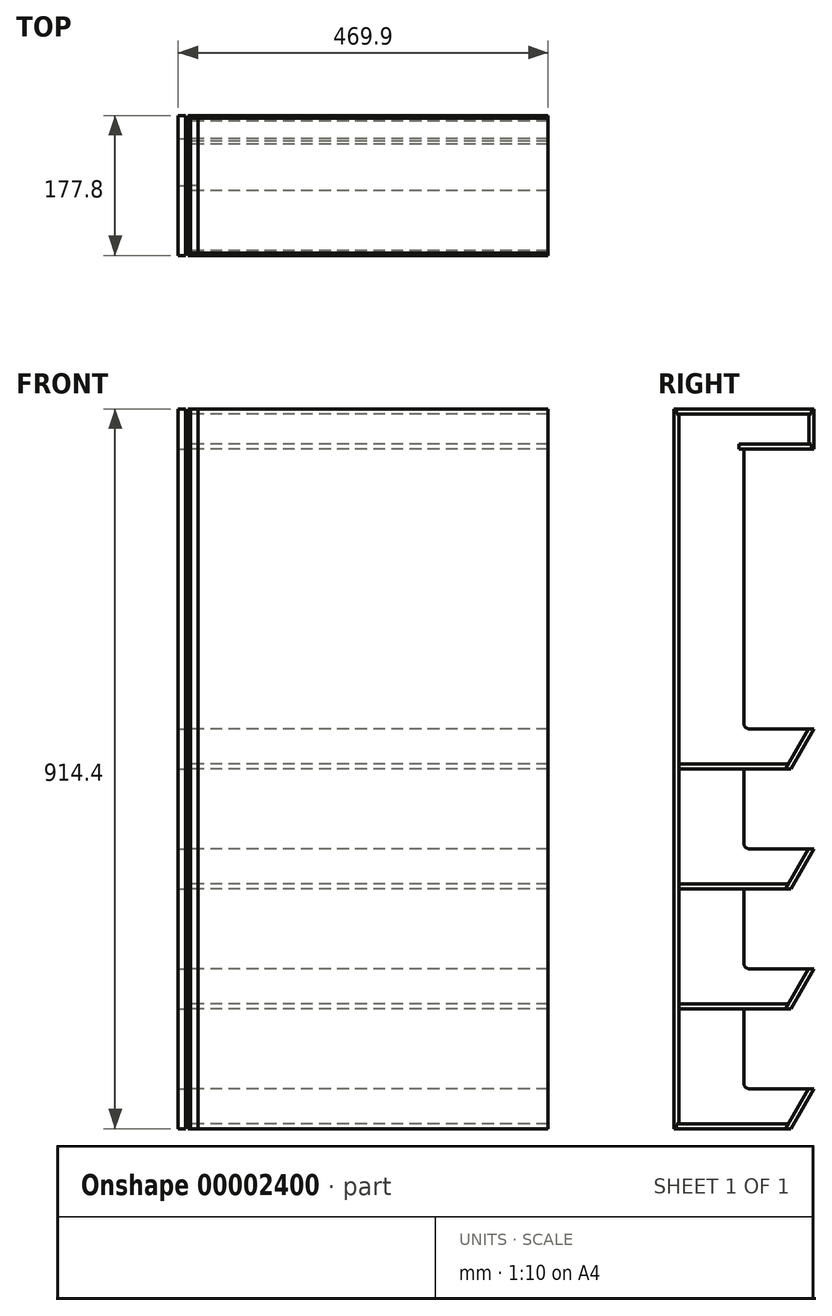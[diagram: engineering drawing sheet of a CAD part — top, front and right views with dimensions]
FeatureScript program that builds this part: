
annotation { "Feature Type Name" : "Feature", "Feature Type Description" : "" }
export const myFeature = defineFeature(function(context is Context, id is Id, definition is map)
    precondition{}
    {
        {
            var Q0;
            Q0=qCreatedBy(makeId("Right.planeOp"),FACE);
            var sketch = newSketch(context, id + "F0", { "sketchPlane" : qUnion([Q0])});
            skLineSegment(sketch, "E0", {"start": v(-132.09, 458.14) * mm, "end": v(-132.09, -456.26) * mm});
            skLineSegment(sketch, "E1", {"start": v(-132.09, -456.26) * mm, "end": v(-43.19, -456.26) * mm});
            skLineSegment(sketch, "E2", {"start": v(-43.19, -456.26) * mm, "end": v(16.38, -456.26) * mm});
            skLineSegment(sketch, "E3", {"start": v(16.38, -456.26) * mm, "end": v(45.71, -405.46) * mm});
            skLineSegment(sketch, "E4", {"start": v(45.71, -405.46) * mm, "end": v(-36.84, -405.46) * mm});
            skLineSegment(sketch, "E5", {"start": v(-43.19, -399.1) * mm, "end": v(-43.19, -303.86) * mm});
            skLineSegment(sketch, "E6", {"start": v(-43.19, -303.86) * mm, "end": v(16.38, -303.86) * mm});
            skLineSegment(sketch, "E7", {"start": v(-43.19, 407.34) * mm, "end": v(-43.19, 58.1) * mm});
            skLineSegment(sketch, "E8", {"start": v(45.71, 51.74) * mm, "end": v(16.38, 0.94) * mm});
            skLineSegment(sketch, "E9", {"start": v(16.38, 0.94) * mm, "end": v(-43.19, 0.94) * mm});
            skLineSegment(sketch, "E10", {"start": v(-43.19, 0.94) * mm, "end": v(-43.19, -94.3) * mm});
            skLineSegment(sketch, "E11", {"start": v(-36.84, -100.66) * mm, "end": v(45.71, -100.66) * mm});
            skLineSegment(sketch, "E12", {"start": v(45.71, -100.66) * mm, "end": v(16.38, -151.46) * mm});
            skLineSegment(sketch, "E13", {"start": v(16.38, -151.46) * mm, "end": v(-43.19, -151.46) * mm});
            skLineSegment(sketch, "E14", {"start": v(-43.19, -151.46) * mm, "end": v(-43.19, -246.7) * mm});
            skLineSegment(sketch, "E15", {"start": v(-36.84, -253.06) * mm, "end": v(45.71, -253.06) * mm});
            skLineSegment(sketch, "E16", {"start": v(45.71, -253.06) * mm, "end": v(16.38, -303.86) * mm});
            skLineSegment(sketch, "E17", {"start": v(-36.84, 51.74) * mm, "end": v(45.71, 51.74) * mm});
            skLineSegment(sketch, "E18", {"start": v(45.71, 458.14) * mm, "end": v(45.71, 407.34) * mm});
            skLineSegment(sketch, "E19", {"start": v(45.71, 407.34) * mm, "end": v(-43.19, 407.34) * mm});
            skLineSegment(sketch, "E20", {"start": v(-132.09, 458.14) * mm, "end": v(45.71, 458.14) * mm});
            skLineSegment(sketch, "E21.0", {"start": v(12.72, 7.3) * mm, "end": v(-49.54, 7.3) * mm});
            skLineSegment(sketch, "E21.1", {"start": v(34.71, 45.4) * mm, "end": v(12.72, 7.3) * mm});
            skLineSegment(sketch, "E21.3", {"start": v(-49.54, 413.7) * mm, "end": v(-49.54, 407.34) * mm});
            skLineSegment(sketch, "E21.4", {"start": v(39.36, 413.7) * mm, "end": v(-49.54, 413.7) * mm});
            skLineSegment(sketch, "E21.6", {"start": v(39.36, 451.8) * mm, "end": v(39.36, 413.7) * mm});
            skLineSegment(sketch, "E21.7", {"start": v(-125.74, 451.8) * mm, "end": v(39.36, 451.8) * mm});
            skLineSegment(sketch, "E21.8", {"start": v(-125.74, 451.8) * mm, "end": v(-125.74, -449.9) * mm});
            skLineSegment(sketch, "E21.9", {"start": v(-125.74, -449.9) * mm, "end": v(-43.19, -449.9) * mm});
            skLineSegment(sketch, "E21.10", {"start": v(-43.19, -449.9) * mm, "end": v(12.72, -449.9) * mm});
            skLineSegment(sketch, "E21.11", {"start": v(12.72, -449.9) * mm, "end": v(34.71, -411.8) * mm});
            skLineSegment(sketch, "E21.14", {"start": v(-49.54, -297.5) * mm, "end": v(12.72, -297.5) * mm});
            skLineSegment(sketch, "E21.15", {"start": v(34.71, -259.4) * mm, "end": v(12.72, -297.5) * mm});
            skLineSegment(sketch, "E21.18", {"start": v(12.72, -145.1) * mm, "end": v(-49.54, -145.1) * mm});
            skLineSegment(sketch, "E21.19", {"start": v(34.71, -107) * mm, "end": v(12.72, -145.1) * mm});
            skLineSegment(sketch, "E22.1", {"start": v(42.54, 454.97) * mm, "end": v(42.54, 451.8) * mm});
            skLineSegment(sketch, "E22.5", {"start": v(-128.91, 454.97) * mm, "end": v(-128.91, 451.8) * mm});
            skLineSegment(sketch, "E23", {"start": v(-125.74, 451.8) * mm, "end": v(-128.91, 451.8) * mm});
            skLineSegment(sketch, "E24", {"start": v(-128.91, 454.97) * mm, "end": v(-128.91, 458.14) * mm});
            skLineSegment(sketch, "E25", {"start": v(39.36, 451.8) * mm, "end": v(42.54, 451.8) * mm});
            skLineSegment(sketch, "E26", {"start": v(42.54, 451.8) * mm, "end": v(42.54, 458.14) * mm});
            skLineSegment(sketch, "E27", {"start": v(-125.74, -449.9) * mm, "end": v(-128.91, -449.9) * mm});
            skLineSegment(sketch, "E28", {"start": v(-128.91, -453.08) * mm, "end": v(-128.91, -456.26) * mm});
            skLineSegment(sketch, "E29.trimOffspring", {"start": v(-128.91, -449.9) * mm, "end": v(-128.91, -453.08) * mm});
            skLineSegment(sketch, "E30", {"start": v(39.36, 413.7) * mm, "end": v(42.54, 413.7) * mm});
            skLineSegment(sketch, "E31", {"start": v(42.54, 413.7) * mm, "end": v(42.54, 407.34) * mm});
            skLineSegment(sketch, "E32.trimOffspring", {"start": v(42.54, 413.7) * mm, "end": v(42.54, 410.52) * mm});
            skLineSegment(sketch, "E33", {"start": v(-43.19, 407.34) * mm, "end": v(-49.54, 407.34) * mm});
            skLineSegment(sketch, "E34", {"start": v(34.71, 45.4) * mm, "end": v(38.38, 51.74) * mm});
            skLineSegment(sketch, "E35", {"start": v(38.38, 51.74) * mm, "end": v(9.05, 0.94) * mm});
            skLineSegment(sketch, "E36", {"start": v(-43.19, 0.94) * mm, "end": v(-49.54, 0.94) * mm});
            skLineSegment(sketch, "E37", {"start": v(34.71, -107) * mm, "end": v(38.38, -100.66) * mm});
            skLineSegment(sketch, "E38", {"start": v(38.38, -100.66) * mm, "end": v(12.72, -145.1) * mm});
            skLineSegment(sketch, "E39", {"start": v(12.72, -145.1) * mm, "end": v(9.05, -151.46) * mm});
            skLineSegment(sketch, "E40", {"start": v(-43.19, -151.46) * mm, "end": v(-49.54, -151.46) * mm});
            skLineSegment(sketch, "E41", {"start": v(34.71, -259.4) * mm, "end": v(38.38, -253.06) * mm});
            skLineSegment(sketch, "E42", {"start": v(38.38, -253.06) * mm, "end": v(12.72, -297.5) * mm});
            skLineSegment(sketch, "E43", {"start": v(9.05, -303.86) * mm, "end": v(-49.54, -303.86) * mm});
            skLineSegment(sketch, "E44", {"start": v(34.71, -411.8) * mm, "end": v(38.38, -405.46) * mm});
            skLineSegment(sketch, "E45", {"start": v(38.38, -405.46) * mm, "end": v(9.05, -456.26) * mm});
            skLineSegment(sketch, "E46", {"start": v(38.38, -253.06) * mm, "end": v(9.05, -303.86) * mm});
            skLineSegment(sketch, "E47", {"start": v(-49.54, -303.86) * mm, "end": v(-125.74, -303.86) * mm});
            skLineSegment(sketch, "E48", {"start": v(-125.74, -303.86) * mm, "end": v(-125.74, -297.5) * mm});
            skLineSegment(sketch, "E49", {"start": v(-125.74, -297.5) * mm, "end": v(-49.54, -297.5) * mm});
            skLineSegment(sketch, "E50", {"start": v(-49.54, -145.1) * mm, "end": v(-125.74, -145.1) * mm});
            skLineSegment(sketch, "E51", {"start": v(-125.74, -145.1) * mm, "end": v(-125.74, -151.46) * mm});
            skLineSegment(sketch, "E52", {"start": v(-125.74, -151.46) * mm, "end": v(-49.54, -151.46) * mm});
            skLineSegment(sketch, "E53", {"start": v(-49.54, 7.3) * mm, "end": v(-125.74, 7.3) * mm});
            skLineSegment(sketch, "E54", {"start": v(-49.54, 0.94) * mm, "end": v(-125.74, 0.94) * mm});
            skPoint(sketch, "E55.visualSharp", {"position": v(-43.19, 51.74) * mm});
            skArc(sketch, "E55.filletArc", {"start": v(-43.19, 58.1) * mm, "mid": v(-41.33, 53.6) * mm, "end": v(-36.84, 51.74) * mm});
            skPoint(sketch, "E56.visualSharp", {"position": v(-43.19, -100.66) * mm});
            skArc(sketch, "E56.filletArc", {"start": v(-43.19, -94.3) * mm, "mid": v(-41.33, -98.8) * mm, "end": v(-36.84, -100.66) * mm});
            skPoint(sketch, "E57.visualSharp", {"position": v(-43.19, -253.06) * mm});
            skArc(sketch, "E57.filletArc", {"start": v(-43.19, -246.7) * mm, "mid": v(-41.33, -251.2) * mm, "end": v(-36.84, -253.06) * mm});
            skPoint(sketch, "E58.visualSharp", {"position": v(-43.19, -405.46) * mm});
            skArc(sketch, "E58.filletArc", {"start": v(-43.19, -399.1) * mm, "mid": v(-41.33, -403.6) * mm, "end": v(-36.84, -405.46) * mm});
            skSolve(sketch);
        }
        {
            var Q0;
            Q0=makeQuery(id+"F0.imprint","IMPRINT",FACE,{"disambiguationData":[TD([[makeQuery(id+"F0.imprint","IMPRINT",EDGE,{"derivedFrom":sQuery(id+"F0.wireOp",EDGE,"E21.0")}),-1.0]])]});
            var Q1;
            Q1=makeQuery(id+"F0.imprint","IMPRINT",FACE,{"disambiguationData":[TD([[makeQuery(id+"F0.imprint","IMPRINT",EDGE,{"derivedFrom":sQuery(id+"F0.wireOp",EDGE,"E0")}),1.0]])]});
            var Q2;
            {var subQ7=sQuery(id+"F0.wireOp",EDGE,"E8");Q2=makeQuery(id+"F0.imprint","IMPRINT",FACE,{"disambiguationData":[TD([[makeQuery(id+"F0.imprint","IMPRINT",EDGE,{"derivedFrom":subQ7}),-1.0]])]});}
            var Q3;
            {var subQ4=sQuery(id+"F0.wireOp",EDGE,"E21.0");Q3=makeQuery(id+"F0.imprint","IMPRINT",FACE,{"disambiguationData":[TD([[makeQuery(id+"F0.imprint","IMPRINT",EDGE,{"derivedFrom":subQ4}),1.0]])]});}
            var Q4;
            {var subQ6=sQuery(id+"F0.wireOp",EDGE,"E12");Q4=makeQuery(id+"F0.imprint","IMPRINT",FACE,{"disambiguationData":[TD([[makeQuery(id+"F0.imprint","IMPRINT",EDGE,{"derivedFrom":subQ6}),-1.0]])]});}
            var Q5;
            Q5=makeQuery(id+"F0.imprint","IMPRINT",FACE,{"disambiguationData":[TD([[makeQuery(id+"F0.imprint","IMPRINT",EDGE,{"derivedFrom":sQuery(id+"F0.wireOp",EDGE,"E21.17")}),1.0]])]});
            var Q6;
            {var subQ3=sQuery(id+"F0.wireOp",EDGE,"E16");Q6=makeQuery(id+"F0.imprint","IMPRINT",FACE,{"disambiguationData":[TD([[makeQuery(id+"F0.imprint","IMPRINT",EDGE,{"derivedFrom":subQ3}),-1.0]])]});}
            var Q7;
            {var subQ7=sQuery(id+"F0.wireOp",EDGE,"E3");Q7=makeQuery(id+"F0.imprint","IMPRINT",FACE,{"disambiguationData":[TD([[makeQuery(id+"F0.imprint","IMPRINT",EDGE,{"derivedFrom":subQ7}),1.0]])]});}
            var Q8;
            {var subQ6=sQuery(id+"F0.wireOp",EDGE,"E18");Q8=makeQuery(id+"F0.imprint","IMPRINT",FACE,{"disambiguationData":[TD([[makeQuery(id+"F0.imprint","IMPRINT",EDGE,{"derivedFrom":subQ6}),-1.0]])]});}
            var Q9;
            Q9=makeQuery(id+"F0.imprint","IMPRINT",FACE,{"disambiguationData":[TD([[makeQuery(id+"F0.imprint","IMPRINT",EDGE,{"derivedFrom":sQuery(id+"F0.wireOp",EDGE,"E21.3")}),1.0]])]});
            var Q10;
            Q10=makeQuery(id+"F0.imprint","IMPRINT",FACE,{"disambiguationData":[TD([[makeQuery(id+"F0.imprint","IMPRINT",EDGE,{"derivedFrom":sQuery(id+"F0.wireOp",EDGE,"E21.7")}),1.0]])]});
            var Q11;
            {var subQ4=sQuery(id+"F0.wireOp",EDGE,"E21.13");Q11=makeQuery(id+"F0.imprint","IMPRINT",FACE,{"disambiguationData":[TD([[makeQuery(id+"F0.imprint","IMPRINT",EDGE,{"derivedFrom":subQ4}),-1.0]])]});}
            var Q12;
            Q12=makeQuery(id+"F0.imprint","IMPRINT",FACE,{"disambiguationData":[TD([[makeQuery(id+"F0.imprint","IMPRINT",EDGE,{"derivedFrom":sQuery(id+"F0.wireOp",EDGE,"E21.9")}),-1.0]])]});
            var Q13;
            {var subQ2=sQuery(id+"F0.wireOp",EDGE,"E21.14");Q13=makeQuery(id+"F0.imprint","IMPRINT",FACE,{"disambiguationData":[TD([[makeQuery(id+"F0.imprint","IMPRINT",EDGE,{"derivedFrom":subQ2}),-1.0]])]});}
            var Q14;
            {var subQ9=sQuery(id+"F0.wireOp",EDGE,"E5");Q14=makeQuery(id+"F0.imprint","IMPRINT",FACE,{"disambiguationData":[TD([[makeQuery(id+"F0.imprint","IMPRINT",EDGE,{"derivedFrom":subQ9}),1.0]])]});}
            var Q15;
            {var subQ8=sQuery(id+"F0.wireOp",EDGE,"E10");Q15=makeQuery(id+"F0.imprint","IMPRINT",FACE,{"disambiguationData":[TD([[makeQuery(id+"F0.imprint","IMPRINT",EDGE,{"derivedFrom":subQ8}),-1.0]])]});}
            var Q16;
            {var subQ8=sQuery(id+"F0.wireOp",EDGE,"E14");Q16=makeQuery(id+"F0.imprint","IMPRINT",FACE,{"disambiguationData":[TD([[makeQuery(id+"F0.imprint","IMPRINT",EDGE,{"derivedFrom":subQ8}),-1.0]])]});}
            var Q17;
            Q17=makeQuery(id+"F0.imprint","IMPRINT",FACE,{"disambiguationData":[TD([[makeQuery(id+"F0.imprint","IMPRINT",EDGE,{"derivedFrom":sQuery(id+"F0.wireOp",EDGE,"E21.18")}),1.0]])]});
            extrude(context, id + "F1", {"entities" : qUnion([Q0, Q1, Q2, Q3, Q4, Q5, Q6, Q7, Q8, Q9, Q10, Q11, Q12, Q13, Q14, Q15, Q16, Q17]), "oppositeDirection" : true, "depth" : 12.7 * mm});
        }
        {
            var Q0;
            Q0=makeQuery(id+"F0.imprint","IMPRINT",FACE,{"disambiguationData":[TD([[makeQuery(id+"F0.imprint","IMPRINT",EDGE,{"derivedFrom":sQuery(id+"F0.wireOp",EDGE,"E0")}),1.0]])]});
            var Q1;
            Q1=makeQuery(id+"F0.imprint","IMPRINT",FACE,{"disambiguationData":[TD([[makeQuery(id+"F0.imprint","IMPRINT",EDGE,{"derivedFrom":sQuery(id+"F0.wireOp",EDGE,"E21.9")}),-1.0]])]});
            var Q2;
            {var subQ7=sQuery(id+"F0.wireOp",EDGE,"E3");Q2=makeQuery(id+"F0.imprint","IMPRINT",FACE,{"disambiguationData":[TD([[makeQuery(id+"F0.imprint","IMPRINT",EDGE,{"derivedFrom":subQ7}),1.0]])]});}
            var Q3;
            {var subQ3=sQuery(id+"F0.wireOp",EDGE,"E16");Q3=makeQuery(id+"F0.imprint","IMPRINT",FACE,{"disambiguationData":[TD([[makeQuery(id+"F0.imprint","IMPRINT",EDGE,{"derivedFrom":subQ3}),-1.0]])]});}
            var Q4;
            Q4=makeQuery(id+"F0.imprint","IMPRINT",FACE,{"disambiguationData":[TD([[makeQuery(id+"F0.imprint","IMPRINT",EDGE,{"derivedFrom":sQuery(id+"F0.wireOp",EDGE,"E21.17")}),1.0]])]});
            var Q5;
            {var subQ6=sQuery(id+"F0.wireOp",EDGE,"E12");Q5=makeQuery(id+"F0.imprint","IMPRINT",FACE,{"disambiguationData":[TD([[makeQuery(id+"F0.imprint","IMPRINT",EDGE,{"derivedFrom":subQ6}),-1.0]])]});}
            var Q6;
            {var subQ4=sQuery(id+"F0.wireOp",EDGE,"E21.0");Q6=makeQuery(id+"F0.imprint","IMPRINT",FACE,{"disambiguationData":[TD([[makeQuery(id+"F0.imprint","IMPRINT",EDGE,{"derivedFrom":subQ4}),1.0]])]});}
            var Q7;
            {var subQ7=sQuery(id+"F0.wireOp",EDGE,"E8");Q7=makeQuery(id+"F0.imprint","IMPRINT",FACE,{"disambiguationData":[TD([[makeQuery(id+"F0.imprint","IMPRINT",EDGE,{"derivedFrom":subQ7}),-1.0]])]});}
            var Q8;
            Q8=makeQuery(id+"F0.imprint","IMPRINT",FACE,{"disambiguationData":[TD([[makeQuery(id+"F0.imprint","IMPRINT",EDGE,{"derivedFrom":sQuery(id+"F0.wireOp",EDGE,"E21.7")}),1.0]])]});
            var Q9;
            {var subQ6=sQuery(id+"F0.wireOp",EDGE,"E18");Q9=makeQuery(id+"F0.imprint","IMPRINT",FACE,{"disambiguationData":[TD([[makeQuery(id+"F0.imprint","IMPRINT",EDGE,{"derivedFrom":subQ6}),-1.0]])]});}
            var Q10;
            Q10=makeQuery(id+"F0.imprint","IMPRINT",FACE,{"disambiguationData":[TD([[makeQuery(id+"F0.imprint","IMPRINT",EDGE,{"derivedFrom":sQuery(id+"F0.wireOp",EDGE,"E21.3")}),1.0]])]});
            var Q11;
            {var subQ4=sQuery(id+"F0.wireOp",EDGE,"E21.13");Q11=makeQuery(id+"F0.imprint","IMPRINT",FACE,{"disambiguationData":[TD([[makeQuery(id+"F0.imprint","IMPRINT",EDGE,{"derivedFrom":subQ4}),-1.0]])]});}
            var Q12;
            {var subQ2=sQuery(id+"F0.wireOp",EDGE,"E21.14");Q12=makeQuery(id+"F0.imprint","IMPRINT",FACE,{"disambiguationData":[TD([[makeQuery(id+"F0.imprint","IMPRINT",EDGE,{"derivedFrom":subQ2}),-1.0]])]});}
            var Q13;
            Q13=makeQuery(id+"F0.imprint","IMPRINT",FACE,{"disambiguationData":[TD([[makeQuery(id+"F0.imprint","IMPRINT",EDGE,{"derivedFrom":sQuery(id+"F0.wireOp",EDGE,"E21.18")}),1.0]])]});
            extrude(context, id + "F2", {"entities" : qUnion([Q0, Q1, Q2, Q3, Q4, Q5, Q6, Q7, Q8, Q9, Q10, Q11, Q12, Q13]), "operationType" : NewBodyOperationType.REMOVE, "oppositeDirection" : true, "depth" : 3.17 * mm});
        }
        {
            var Q0;
            Q0=makeQuery(id+"F1.opExtrude","SWEPT_BODY",BODY,{"disambiguationData":[OSD([sQuery(id+"F0.wireOp",EDGE,"E0"),sQuery(id+"F0.wireOp",EDGE,"E1"),sQuery(id+"F0.wireOp",EDGE,"E2"),sQuery(id+"F0.wireOp",EDGE,"E3"),sQuery(id+"F0.wireOp",EDGE,"E4"),sQuery(id+"F0.wireOp",EDGE,"E5"),sQuery(id+"F0.wireOp",EDGE,"E6"),sQuery(id+"F0.wireOp",EDGE,"E7"),sQuery(id+"F0.wireOp",EDGE,"E8"),sQuery(id+"F0.wireOp",EDGE,"E9"),sQuery(id+"F0.wireOp",EDGE,"E10"),sQuery(id+"F0.wireOp",EDGE,"E11"),sQuery(id+"F0.wireOp",EDGE,"E12"),sQuery(id+"F0.wireOp",EDGE,"E13"),sQuery(id+"F0.wireOp",EDGE,"E14"),sQuery(id+"F0.wireOp",EDGE,"E15"),sQuery(id+"F0.wireOp",EDGE,"E16"),sQuery(id+"F0.wireOp",EDGE,"E17"),sQuery(id+"F0.wireOp",EDGE,"E18"),sQuery(id+"F0.wireOp",EDGE,"E19"),sQuery(id+"F0.wireOp",EDGE,"E20"),sQuery(id+"F0.wireOp",EDGE,"E43"),sQuery(id+"F0.wireOp",EDGE,"E55.filletArc"),sQuery(id+"F0.wireOp",EDGE,"E56.filletArc"),sQuery(id+"F0.wireOp",EDGE,"E57.filletArc"),sQuery(id+"F0.wireOp",EDGE,"E58.filletArc")])]});
            var Q1;
            Q1=qCreatedBy(makeId("Right.planeOp"),FACE);
            mirror(context, id + "F3", {"entities" : qUnion([Q0]), "mirrorPlane" : qUnion([Q1])});
        }
        {
            var Q0;
            {var subQ3=sQuery(id+"F0.wireOp",EDGE,"E0");Q0=makeQuery(id+"F0.imprint","IMPRINT",FACE,{"disambiguationData":[TD([[makeQuery(id+"F0.imprint","IMPRINT",EDGE,{"derivedFrom":subQ3}),1.0]])]});}
            extrude(context, id + "F4", {"entities" : qUnion([Q0]), "depth" : 457.2 * mm});
        }
        {
            var Q0;
            Q0=makeQuery(id+"F0.imprint","IMPRINT",FACE,{"disambiguationData":[TD([[makeQuery(id+"F0.imprint","IMPRINT",EDGE,{"derivedFrom":sQuery(id+"F0.wireOp",EDGE,"E21.9")}),-1.0]])]});
            extrude(context, id + "F5", {"entities" : qUnion([Q0]), "depth" : 457.2 * mm});
        }
        {
            var Q0;
            {var subQ7=sQuery(id+"F0.wireOp",EDGE,"E3");Q0=makeQuery(id+"F0.imprint","IMPRINT",FACE,{"disambiguationData":[TD([[makeQuery(id+"F0.imprint","IMPRINT",EDGE,{"derivedFrom":subQ7}),1.0]])]});}
            extrude(context, id + "F6", {"entities" : qUnion([Q0]), "depth" : 457.2 * mm});
        }
        {
            var Q0;
            {var subQ2=sQuery(id+"F0.wireOp",EDGE,"E21.14");Q0=makeQuery(id+"F0.imprint","IMPRINT",FACE,{"disambiguationData":[TD([[makeQuery(id+"F0.imprint","IMPRINT",EDGE,{"derivedFrom":subQ2}),-1.0]])]});}
            extrude(context, id + "F7", {"entities" : qUnion([Q0]), "depth" : 457.2 * mm});
        }
        {
            var Q0;
            {var subQ2=sQuery(id+"F0.wireOp",EDGE,"E6");Q0=makeQuery(id+"F0.imprint","IMPRINT",FACE,{"disambiguationData":[TD([[makeQuery(id+"F0.imprint","IMPRINT",EDGE,{"derivedFrom":subQ2}),1.0]])]});}
            extrude(context, id + "F8", {"entities" : qUnion([Q0]), "depth" : 457.2 * mm});
        }
        {
            var Q0;
            Q0=makeQuery(id+"F0.imprint","IMPRINT",FACE,{"disambiguationData":[TD([[makeQuery(id+"F0.imprint","IMPRINT",EDGE,{"derivedFrom":sQuery(id+"F0.wireOp",EDGE,"E21.18")}),1.0]])]});
            extrude(context, id + "F9", {"entities" : qUnion([Q0]), "depth" : 457.2 * mm});
        }
        {
            var Q0;
            {var subQ6=sQuery(id+"F0.wireOp",EDGE,"E12");Q0=makeQuery(id+"F0.imprint","IMPRINT",FACE,{"disambiguationData":[TD([[makeQuery(id+"F0.imprint","IMPRINT",EDGE,{"derivedFrom":subQ6}),-1.0]])]});}
            extrude(context, id + "F10", {"entities" : qUnion([Q0]), "depth" : 457.2 * mm});
        }
        {
            var Q0;
            {var subQ4=sQuery(id+"F0.wireOp",EDGE,"E21.0");Q0=makeQuery(id+"F0.imprint","IMPRINT",FACE,{"disambiguationData":[TD([[makeQuery(id+"F0.imprint","IMPRINT",EDGE,{"derivedFrom":subQ4}),1.0]])]});}
            extrude(context, id + "F11", {"entities" : qUnion([Q0]), "depth" : 457.2 * mm});
        }
        {
            var Q0;
            {var subQ7=sQuery(id+"F0.wireOp",EDGE,"E8");Q0=makeQuery(id+"F0.imprint","IMPRINT",FACE,{"disambiguationData":[TD([[makeQuery(id+"F0.imprint","IMPRINT",EDGE,{"derivedFrom":subQ7}),-1.0]])]});}
            extrude(context, id + "F12", {"entities" : qUnion([Q0]), "depth" : 457.2 * mm});
        }
        {
            var Q0;
            Q0=makeQuery(id+"F0.imprint","IMPRINT",FACE,{"disambiguationData":[TD([[makeQuery(id+"F0.imprint","IMPRINT",EDGE,{"derivedFrom":sQuery(id+"F0.wireOp",EDGE,"E21.3")}),1.0]])]});
            extrude(context, id + "F13", {"entities" : qUnion([Q0]), "depth" : 457.2 * mm});
        }
        {
            var Q0;
            {var subQ6=sQuery(id+"F0.wireOp",EDGE,"E18");Q0=makeQuery(id+"F0.imprint","IMPRINT",FACE,{"disambiguationData":[TD([[makeQuery(id+"F0.imprint","IMPRINT",EDGE,{"derivedFrom":subQ6}),-1.0]])]});}
            extrude(context, id + "F14", {"entities" : qUnion([Q0]), "depth" : 457.2 * mm});
        }
        {
            var Q0;
            Q0=makeQuery(id+"F0.imprint","IMPRINT",FACE,{"disambiguationData":[TD([[makeQuery(id+"F0.imprint","IMPRINT",EDGE,{"derivedFrom":sQuery(id+"F0.wireOp",EDGE,"E21.7")}),1.0]])]});
            extrude(context, id + "F15", {"entities" : qUnion([Q0]), "depth" : 457.2 * mm});
        }
    });
